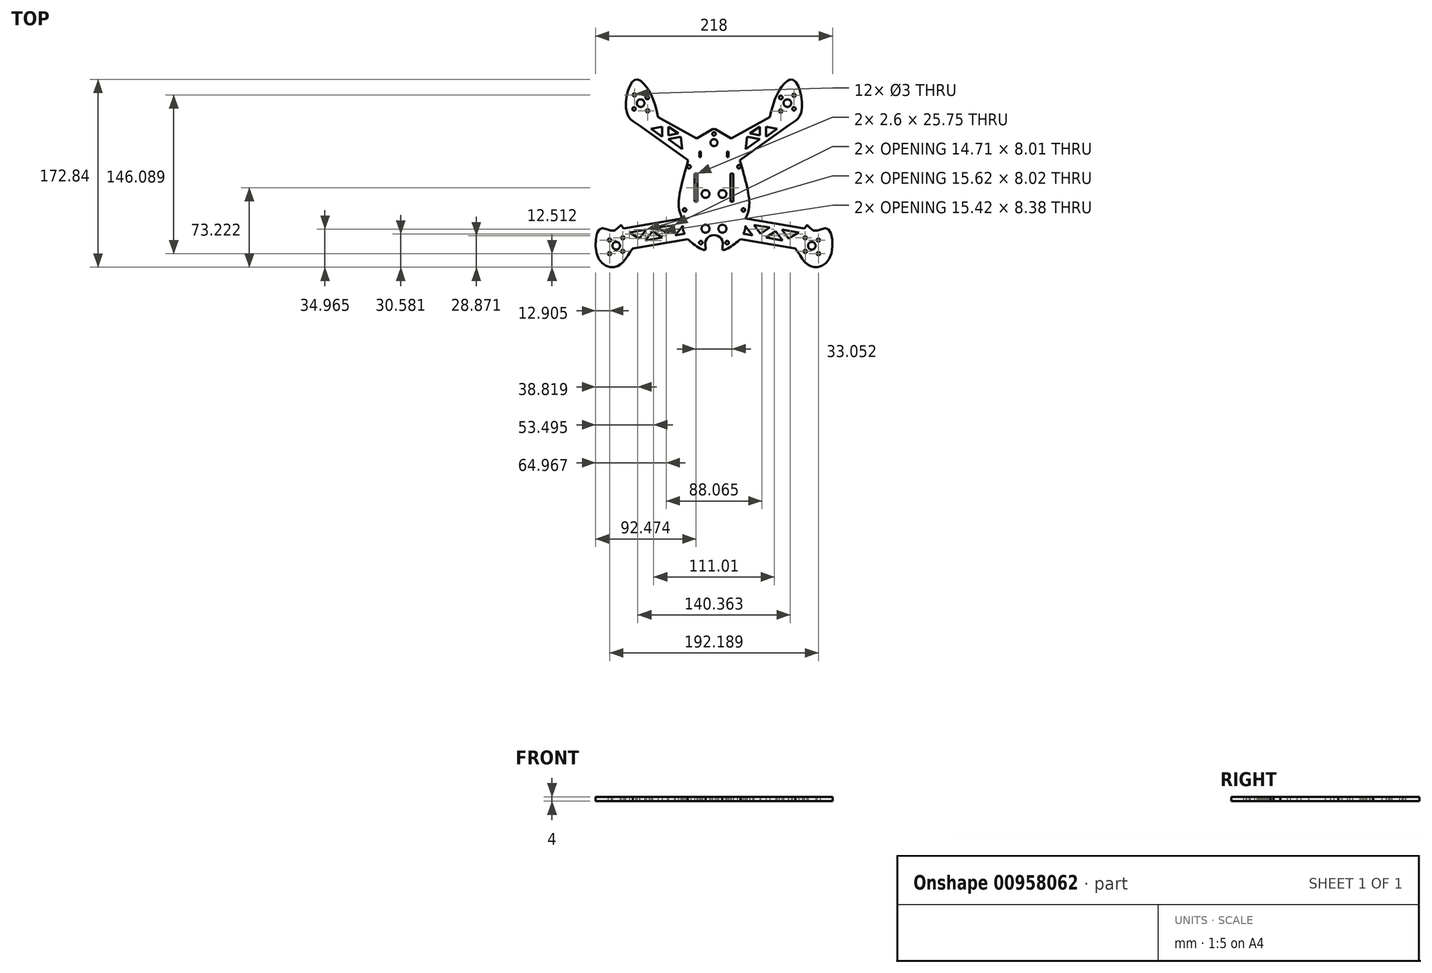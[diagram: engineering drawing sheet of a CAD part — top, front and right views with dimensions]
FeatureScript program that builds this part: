
annotation { "Feature Type Name" : "Feature", "Feature Type Description" : "" }
export const myFeature = defineFeature(function(context is Context, id is Id, definition is map)
    precondition{}
    {
        {
            var Q0;
            Q0=qCreatedBy(makeId("Top.planeOp"),FACE);
            var sketch = newSketch(context, id + "F0", { "sketchPlane" : qUnion([Q0])});
            skCircle(sketch, "E0", {"center": v(-90, -29.8) * mm, "radius": 3.5 * mm});
            skCircle(sketch, "E1", {"center": v(-96.1, -37.08) * mm, "radius": 1.5 * mm});
            skCircle(sketch, "E2", {"center": v(-83.9, -22.5) * mm, "radius": 1.5 * mm});
            skCircle(sketch, "E3", {"center": v(-96.07, -24.58) * mm, "radius": 1.5 * mm});
            skCircle(sketch, "E4", {"center": v(-83.93, -35) * mm, "radius": 1.5 * mm});
            skCircle(sketch, "E5.MirrorC", {"center": v(96.1, -37.08) * mm, "radius": 1.5 * mm});
            skCircle(sketch, "E6.MirrorC", {"center": v(83.93, -35) * mm, "radius": 1.5 * mm});
            skCircle(sketch, "E7.MirrorC", {"center": v(83.9, -22.5) * mm, "radius": 1.5 * mm});
            skCircle(sketch, "E8.MirrorC", {"center": v(96.07, -24.58) * mm, "radius": 1.5 * mm});
            skCircle(sketch, "E9.MirrorC", {"center": v(90, -29.8) * mm, "radius": 3.5 * mm});
            skCircle(sketch, "E10", {"center": v(67.5, 101.43) * mm, "radius": 3.5 * mm});
            skCircle(sketch, "E11", {"center": v(61.4, 94.14) * mm, "radius": 1.5 * mm});
            skCircle(sketch, "E12", {"center": v(73.6, 108.72) * mm, "radius": 1.5 * mm});
            skCircle(sketch, "E13", {"center": v(61.43, 106.64) * mm, "radius": 1.65 * mm});
            skCircle(sketch, "E14", {"center": v(73.57, 96.22) * mm, "radius": 1.54 * mm});
            skCircle(sketch, "E15.MirrorC", {"center": v(-61.05, 94.45) * mm, "radius": 1.5 * mm});
            skCircle(sketch, "E16.MirrorC", {"center": v(-73.52, 96.17) * mm, "radius": 1.54 * mm});
            skCircle(sketch, "E17.MirrorC", {"center": v(-73.22, 109.01) * mm, "radius": 1.5 * mm});
            skCircle(sketch, "E18.MirrorC", {"center": v(-61.43, 106.64) * mm, "radius": 1.65 * mm});
            skCircle(sketch, "E19.MirrorC", {"center": v(-67.5, 101.43) * mm, "radius": 3.5 * mm});
            skLineSegment(sketch, "E20", {"start": v(-83.26, -13.8) * mm, "end": v(-29.18, -4.57) * mm});
            skLineSegment(sketch, "E21", {"start": v(-74.8, -32.33) * mm, "end": v(-24.23, -23.7) * mm});
            skLineSegment(sketch, "E22.MirrorCS", {"start": v(83.26, -13.8) * mm, "end": v(29.18, -4.57) * mm});
            skLineSegment(sketch, "E23.MirrorCS", {"start": v(74.8, -32.33) * mm, "end": v(24.23, -23.7) * mm});
            skFitSpline(sketch, "E24", {"points": [v(83.26, -13.8) * mm, v(90.69, -15.53) * mm, v(104, -13.8) * mm, v(106.85, -40.28) * mm, v(92.32, -49.56) * mm, v(83.26, -44.36) * mm, v(74.8, -32.33) * mm], "startDerivative": vector(48.4, 165.36) * mm, "endDerivative": vector(-54.7, 69.22) * mm});
            skFitSpline(sketch, "E25.MirrorCS", {"points": [v(-83.26, -13.8) * mm, v(-90.69, -15.53) * mm, v(-104, -13.8) * mm, v(-106.85, -40.28) * mm, v(-92.32, -49.56) * mm, v(-83.26, -44.36) * mm, v(-74.8, -32.33) * mm], "startDerivative": vector(-48.4, 165.36) * mm, "endDerivative": vector(54.7, 69.22) * mm});
            skLineSegment(sketch, "E26", {"start": v(-68.28, 80.75) * mm, "end": v(-23.77, 48.85) * mm});
            skLineSegment(sketch, "E27", {"start": v(-51.38, 88.72) * mm, "end": v(-15.87, 68.91) * mm});
            skFitSpline(sketch, "E28", {"points": [v(-68.28, 80.75) * mm, v(-80.38, 93.36) * mm, v(-73.14, 122.75) * mm, v(-60.82, 114.46) * mm, v(-51.38, 88.72) * mm], "startDerivative": vector(-63.76, 40.55) * mm, "endDerivative": vector(23.21, -100.38) * mm});
            skLineSegment(sketch, "E29.MirrorCS", {"start": v(51.38, 88.72) * mm, "end": v(15.87, 68.91) * mm});
            skLineSegment(sketch, "E30.MirrorCS", {"start": v(68.28, 80.75) * mm, "end": v(23.77, 48.85) * mm});
            skFitSpline(sketch, "E31.MirrorCS", {"points": [v(68.28, 80.75) * mm, v(80.38, 93.36) * mm, v(73.14, 122.75) * mm, v(60.82, 114.46) * mm, v(51.38, 88.72) * mm], "startDerivative": vector(63.76, 40.55) * mm, "endDerivative": vector(-23.21, -100.38) * mm});
            skFitSpline(sketch, "E32", {"points": [v(-29.18, -4.57) * mm, v(-32.5, 7.93) * mm, v(-23.77, 48.85) * mm], "startDerivative": vector(-13.42, 29.87) * mm, "endDerivative": vector(20.99, 72.88) * mm});
            skLineSegment(sketch, "E33", {"start": v(-15.87, 68.91) * mm, "end": v(-1.3, 77.4) * mm});
            skLineSegment(sketch, "E34", {"start": v(-1.3, 77.4) * mm, "end": v(0, 77.4) * mm});
            skLineSegment(sketch, "E35.MirrorCS", {"start": v(15.87, 68.91) * mm, "end": v(1.3, 77.4) * mm});
            skLineSegment(sketch, "E36.MirrorCS", {"start": v(1.3, 77.4) * mm, "end": v(0, 77.4) * mm});
            skFitSpline(sketch, "E37.MirrorCS", {"points": [v(29.18, -4.57) * mm, v(32.5, 7.93) * mm, v(23.77, 48.85) * mm], "startDerivative": vector(13.42, 29.87) * mm, "endDerivative": vector(-20.99, 72.88) * mm});
            skFitSpline(sketch, "E38", {"points": [v(-24.23, -23.7) * mm, v(-15.08, -30.83) * mm, v(-8, -33.43) * mm, v(-8, -26.5) * mm, v(0, -20.01) * mm], "startDerivative": vector(27.48, -26.26) * mm, "endDerivative": vector(47.09, 0) * mm});
            skFitSpline(sketch, "E39.MirrorCS", {"points": [v(24.23, -23.7) * mm, v(15.08, -30.83) * mm, v(8, -33.43) * mm, v(8, -26.5) * mm, v(0, -20.01) * mm], "startDerivative": vector(-27.48, -26.26) * mm, "endDerivative": vector(-47.09, 0) * mm});
            skCircle(sketch, "E40", {"center": v(-12.12, -26.95) * mm, "radius": 1.56 * mm});
            skCircle(sketch, "E41", {"center": v(-27.03, 3.13) * mm, "radius": 1.56 * mm});
            skCircle(sketch, "E42", {"center": v(-22.94, 42.94) * mm, "radius": 1.58 * mm});
            skCircle(sketch, "E43", {"center": v(0, 73.16) * mm, "radius": 1.56 * mm});
            skPoint(sketch, "E43.centerSnap0", {"position": v(-8.58, 73.16) * mm});
            skLineSegment(sketch, "E44", {"start": v(-15.23, 17.22) * mm, "end": v(-15.23, 36.5) * mm});
            skLineSegment(sketch, "E45", {"start": v(-15.23, 36.5) * mm, "end": v(-17.82, 36.5) * mm});
            skLineSegment(sketch, "E46", {"start": v(-17.82, 36.5) * mm, "end": v(-17.82, 10.76) * mm});
            skLineSegment(sketch, "E47", {"start": v(-17.82, 10.76) * mm, "end": v(-15.23, 10.76) * mm});
            skLineSegment(sketch, "E48", {"start": v(-15.23, 10.76) * mm, "end": v(-15.23, 17.22) * mm});
            skLineSegment(sketch, "E49.MirrorCS", {"start": v(15.23, 17.22) * mm, "end": v(15.23, 36.5) * mm});
            skLineSegment(sketch, "E50.MirrorCS", {"start": v(15.23, 10.76) * mm, "end": v(15.23, 17.22) * mm});
            skLineSegment(sketch, "E51.MirrorCS", {"start": v(17.82, 36.5) * mm, "end": v(17.82, 10.76) * mm});
            skLineSegment(sketch, "E52.MirrorCS", {"start": v(15.23, 36.5) * mm, "end": v(17.82, 36.5) * mm});
            skLineSegment(sketch, "E53.MirrorCS", {"start": v(17.82, 10.76) * mm, "end": v(15.23, 10.76) * mm});
            skCircle(sketch, "E54.MirrorC", {"center": v(27.03, 3.13) * mm, "radius": 1.56 * mm});
            skCircle(sketch, "E55.MirrorC", {"center": v(22.94, 42.94) * mm, "radius": 1.58 * mm});
            skCircle(sketch, "E56.MirrorC", {"center": v(12.12, -26.95) * mm, "radius": 1.56 * mm});
            skLineSegment(sketch, "E57", {"start": v(-78, -17.66) * mm, "end": v(-68.66, -23.02) * mm});
            skLineSegment(sketch, "E58", {"start": v(-68.66, -23.02) * mm, "end": v(-62.37, -15) * mm});
            skLineSegment(sketch, "E59", {"start": v(-63.22, -24.91) * mm, "end": v(-56.64, -16.53) * mm});
            skLineSegment(sketch, "E60", {"start": v(-56.64, -16.53) * mm, "end": v(-47.8, -22.28) * mm});
            skLineSegment(sketch, "E61", {"start": v(-51.39, -13.13) * mm, "end": v(-42.93, -18.63) * mm});
            skLineSegment(sketch, "E62", {"start": v(-42.93, -18.63) * mm, "end": v(-36.68, -10.62) * mm});
            skLineSegment(sketch, "E63", {"start": v(-35.6, -20.2) * mm, "end": v(-28.66, -11.31) * mm});
            skFitSpline(sketch, "E64", {"points": [v(-28.66, -11.31) * mm, v(-28.66, -14.3) * mm, v(-27.03, -18.74) * mm], "startDerivative": vector(-0.77, -9.34) * mm, "endDerivative": vector(3.49, -6.3) * mm});
            skLineSegment(sketch, "E65", {"start": v(-63.22, -24.91) * mm, "end": v(-47.8, -22.28) * mm});
            skLineSegment(sketch, "E66", {"start": v(-35.6, -20.2) * mm, "end": v(-27.03, -18.74) * mm});
            skLineSegment(sketch, "E67", {"start": v(-36.68, -10.62) * mm, "end": v(-51.39, -13.13) * mm});
            skLineSegment(sketch, "E68", {"start": v(-62.37, -15) * mm, "end": v(-78, -17.66) * mm});
            skLineSegment(sketch, "E69.MirrorCS", {"start": v(78, -17.66) * mm, "end": v(68.66, -23.02) * mm});
            skLineSegment(sketch, "E70.MirrorCS", {"start": v(35.6, -20.2) * mm, "end": v(27.03, -18.74) * mm});
            skLineSegment(sketch, "E71.MirrorCS", {"start": v(56.64, -16.53) * mm, "end": v(47.8, -22.28) * mm});
            skLineSegment(sketch, "E72.MirrorCS", {"start": v(42.93, -18.63) * mm, "end": v(36.68, -10.62) * mm});
            skFitSpline(sketch, "E73.MirrorCS", {"points": [v(28.66, -11.31) * mm, v(28.66, -14.3) * mm, v(27.03, -18.74) * mm], "startDerivative": vector(0.77, -9.34) * mm, "endDerivative": vector(-3.49, -6.3) * mm});
            skLineSegment(sketch, "E74.MirrorCS", {"start": v(36.68, -10.62) * mm, "end": v(51.39, -13.13) * mm});
            skLineSegment(sketch, "E75.MirrorCS", {"start": v(62.37, -15) * mm, "end": v(78, -17.66) * mm});
            skLineSegment(sketch, "E76.MirrorCS", {"start": v(51.39, -13.13) * mm, "end": v(42.93, -18.63) * mm});
            skLineSegment(sketch, "E77.MirrorCS", {"start": v(35.6, -20.2) * mm, "end": v(28.66, -11.31) * mm});
            skLineSegment(sketch, "E78.MirrorCS", {"start": v(63.22, -24.91) * mm, "end": v(56.64, -16.53) * mm});
            skLineSegment(sketch, "E79.MirrorCS", {"start": v(63.22, -24.91) * mm, "end": v(47.8, -22.28) * mm});
            skLineSegment(sketch, "E80.MirrorCS", {"start": v(68.66, -23.02) * mm, "end": v(62.37, -15) * mm});
            skLineSegment(sketch, "E81", {"start": v(-57.9, 77.94) * mm, "end": v(-47.73, 70.52) * mm});
            skLineSegment(sketch, "E82", {"start": v(-42.05, 68.29) * mm, "end": v(-29.28, 59.13) * mm});
            skLineSegment(sketch, "E83", {"start": v(-57.9, 77.94) * mm, "end": v(-47.73, 79.88) * mm});
            skLineSegment(sketch, "E84", {"start": v(-47.73, 79.88) * mm, "end": v(-47.73, 70.52) * mm});
            skLineSegment(sketch, "E85", {"start": v(-42.05, 68.29) * mm, "end": v(-30.42, 70.52) * mm});
            skLineSegment(sketch, "E86", {"start": v(-30.42, 70.52) * mm, "end": v(-29.28, 59.13) * mm});
            skLineSegment(sketch, "E87", {"start": v(-42.05, 79.67) * mm, "end": v(-32.82, 73.58) * mm});
            skLineSegment(sketch, "E88", {"start": v(-32.82, 73.58) * mm, "end": v(-42.05, 71.8) * mm});
            skLineSegment(sketch, "E89", {"start": v(-42.05, 71.8) * mm, "end": v(-42.05, 79.67) * mm});
            skLineSegment(sketch, "E90.MirrorCS", {"start": v(57.9, 77.94) * mm, "end": v(47.73, 79.88) * mm});
            skLineSegment(sketch, "E91.MirrorCS", {"start": v(57.9, 77.94) * mm, "end": v(47.73, 70.52) * mm});
            skLineSegment(sketch, "E92.MirrorCS", {"start": v(47.73, 79.88) * mm, "end": v(47.73, 70.52) * mm});
            skLineSegment(sketch, "E93.MirrorCS", {"start": v(42.05, 71.8) * mm, "end": v(42.05, 79.67) * mm});
            skLineSegment(sketch, "E94.MirrorCS", {"start": v(42.05, 79.67) * mm, "end": v(32.82, 73.58) * mm});
            skLineSegment(sketch, "E95.MirrorCS", {"start": v(32.82, 73.58) * mm, "end": v(42.05, 71.8) * mm});
            skLineSegment(sketch, "E96.MirrorCS", {"start": v(42.05, 68.29) * mm, "end": v(30.42, 70.52) * mm});
            skLineSegment(sketch, "E97.MirrorCS", {"start": v(42.05, 68.29) * mm, "end": v(29.28, 59.13) * mm});
            skLineSegment(sketch, "E98.MirrorCS", {"start": v(30.42, 70.52) * mm, "end": v(29.28, 59.13) * mm});
            skCircle(sketch, "E99", {"center": v(0, 65.06) * mm, "radius": 3.2 * mm});
            skCircle(sketch, "E100", {"center": v(-7.78, 17.85) * mm, "radius": 3.62 * mm});
            skCircle(sketch, "E101", {"center": v(-7.78, -14.15) * mm, "radius": 3.68 * mm});
            skCircle(sketch, "E102.MirrorC", {"center": v(7.78, 17.85) * mm, "radius": 3.62 * mm});
            skCircle(sketch, "E103.MirrorC", {"center": v(7.78, -14.15) * mm, "radius": 3.68 * mm});
            skLineSegment(sketch, "E104", {"start": v(-13.3, 56.85) * mm, "end": v(-13.3, 51.85) * mm});
            skLineSegment(sketch, "E105", {"start": v(-13.3, 51.85) * mm, "end": v(-12, 51.85) * mm});
            skLineSegment(sketch, "E106", {"start": v(-12, 51.85) * mm, "end": v(-12, 56.85) * mm});
            skLineSegment(sketch, "E107", {"start": v(-12, 56.85) * mm, "end": v(-13.3, 56.85) * mm});
            skLineSegment(sketch, "E108.MirrorCS", {"start": v(12, 56.85) * mm, "end": v(13.3, 56.85) * mm});
            skLineSegment(sketch, "E109.MirrorCS", {"start": v(13.3, 51.85) * mm, "end": v(12, 51.85) * mm});
            skLineSegment(sketch, "E110.MirrorCS", {"start": v(12, 51.85) * mm, "end": v(12, 56.85) * mm});
            skLineSegment(sketch, "E111.MirrorCS", {"start": v(13.3, 56.85) * mm, "end": v(13.3, 51.85) * mm});
            skSolve(sketch);
        }
        {
            var Q0;
            Q0=qSketchRegion(id+"F0",true);
            extrude(context, id + "F1", {"entities" : qUnion([Q0]), "depth" : 4 * mm, "offsetDistance" : 25 * mm});
        }
    });
